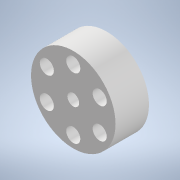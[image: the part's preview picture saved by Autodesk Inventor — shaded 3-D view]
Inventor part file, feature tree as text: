
AUTODESK INVENTOR PART (.ipt)
format: ipt  version: 2021 (Build 250183000, 183)  size: 112,640 bytes
history: native  units: mm
features: other x3, sketch x2, plane x1, extrude x1, reference x1
ambient origin geometry x8: Origin, YZ Plane, XZ Plane, XY Plane, X Axis, Y Axis, Z Axis, Center Point
bodies: Solid1 (feature_tree)
feature tree (8):
  sketch  "Sketch1"  dims[d0=10.0mm d1=0.0mm]
  sketch  "Sketch2"
  plane  "Work Plane1"
  extrude  "Extrusion1"  [1 undecoded]
  reference  "Reference1"
  parser-record x1  (decoder bookkeeping rows leaked as tree rows — omitted from the tree; the rows remain in map.json)
  other  "ilmbt_3d_v1.iam"
  other  "servo shaft flange:1"
note: 1 required parameter value undecoded (feature->parameter linkage not recoverable at this tier; creation-order binding heuristic only, values carry confidence <= 0.55)
note: 1 file-system path scrubbed to <path> (originals preserved in map.json)
